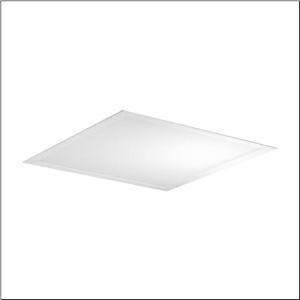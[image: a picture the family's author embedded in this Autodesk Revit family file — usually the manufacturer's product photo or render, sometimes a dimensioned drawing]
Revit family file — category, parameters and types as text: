
# Revit family: apollon_r__21_square_51mq11w72414_6b47
name_source: partatom
category: Lighting Fixtures
units: mm (PartAtom-declared; Revit-internal decimal feet)

## family parameters
Cut with Voids When Loaded = No
Host = Face
Light Source = No
Part Type = Normal
Room Calculation Point = No
Round Connector Dimension = Use Diameter
Shared = No

## types (1)
- Apollon® 21 square (1 x LED, 4200 lm, 23.3 W, 4000K)
    Apparent Load = 23 VA
    CIE Flux Codes = 60 87 97 100 100
    Color Rendering = 80
    Color Temperature = 4000K
    Default Elevation = 1800 mm
    Description = Apollon® 21 square, office luminaire, primary optical cover: micro prismatic cover, of PMMA, CAT 2 (L<= 3000cd/m²), light emission: direct distribution, primary light characteristic: symmetric, installation type: lay-in mounting, LED, rated luminous flux: 4.200lm, luminous efficacy: 180lm/W, light colour: 840, colour temperature: 4000K, with terminal, 3-pole, mains connection: 220..240V, AC/DC, 0/50..60Hz, rated input power: 23.3W, housing, of aluminium, coated, traffic white (RAL 9016), module: M625, length: 620mm, width: 620mm, height: 30mm, housing upper side, of sheet steel, galvanised, protection rating (complete): IP20, protection rating (lamp compartment, on room side): IP50, insulation class (complete): insulation class II (safety insulation), certification: CE, ENEC, impact resistance: IK03, permissible operating ambient temperature: -20..+45°C, permissible storage temperature: -40..+80°C, packaging unit: 1 piece
    Height = 0 mm  [stored 0 ft]
    Lamp = 1 x LED
    Lamp Light Flux = 4200 lm
    Lamp Power = 23.3 W
    Lamp count = 1
    Length = 620 mm
    Luminous efficacy = 180 lm/W
    Manufacturer = Siteco
    ModVariant = No
    Model = 51MQ11W72414
    Mounting Place = Ceiling
    Mounting Type = Recessed
    Number of Poles = 1
    OnlyDefault = Yes
    Power Factor = 1
    Product Name = Apollon® 21 square
    Product group = office luminaire | ceiling recessed
    ProductGroupID = 401
    Protection Class = Protection class II
    Protection Degree = IP 20
    RLX_Detail_Level = 1
    RLX_Emergency_Light_Flux = 0 lm
    RLX_Emergency_Type = 0
    RLX_Emergency_Type_DB = No
    RlxData = <blob elided: 12945 chars, md5=3c3d2722>
    Socket = socket
    Standby Power = 0 W
    System Light Flux = 4200 lm
    System Power = 23 W
    Type Comments = Product without accessories
    Type Image = l_1291054.jpg
    URL = http://relux.com
    VarID = ---
    Voltage = 0 V
    Weight = 0.00 kg
    Width = 620 mm

note: [stored X ft] marks values corroborated as IEEE doubles in the binary element streams (Revit-internal decimal feet)

## geometry (parser evidence)
native form markers: Sweep x12
no freeform markers — native parametric forms only
